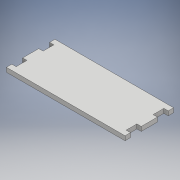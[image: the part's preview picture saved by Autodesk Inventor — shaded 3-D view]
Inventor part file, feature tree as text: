
AUTODESK INVENTOR PART (.ipt)
format: ipt  version: 2018 (Build 220112000, 112)  size: 124,416 bytes
history: native  units: mm
features: extrude x2, sketch x2, plane x1, mirror x1
ambient origin geometry x8: Origin, YZ Plane, XZ Plane, XY Plane, X Axis, Y Axis, Z Axis, Center Point
bodies: Solid1 (feature_tree)
feature tree (6):
  extrude  "Extrusion1"  Depth=45.0mm
  extrude  "Extrusion2"  Depth=4.0mm
  plane  "Work Plane2"
  mirror  "Mirror1"
  sketch  "Sketch1"  dims[d0=110.0mm d1=45.0mm]
  sketch  "Sketch2"  dims[d2=4.0mm d3=0.0mm d4=4.0mm d5=10.0mm d6=4.0mm d7=10.0mm d8=5.0mm d9=5.0mm d10=4.0mm d11=0.0mm]
